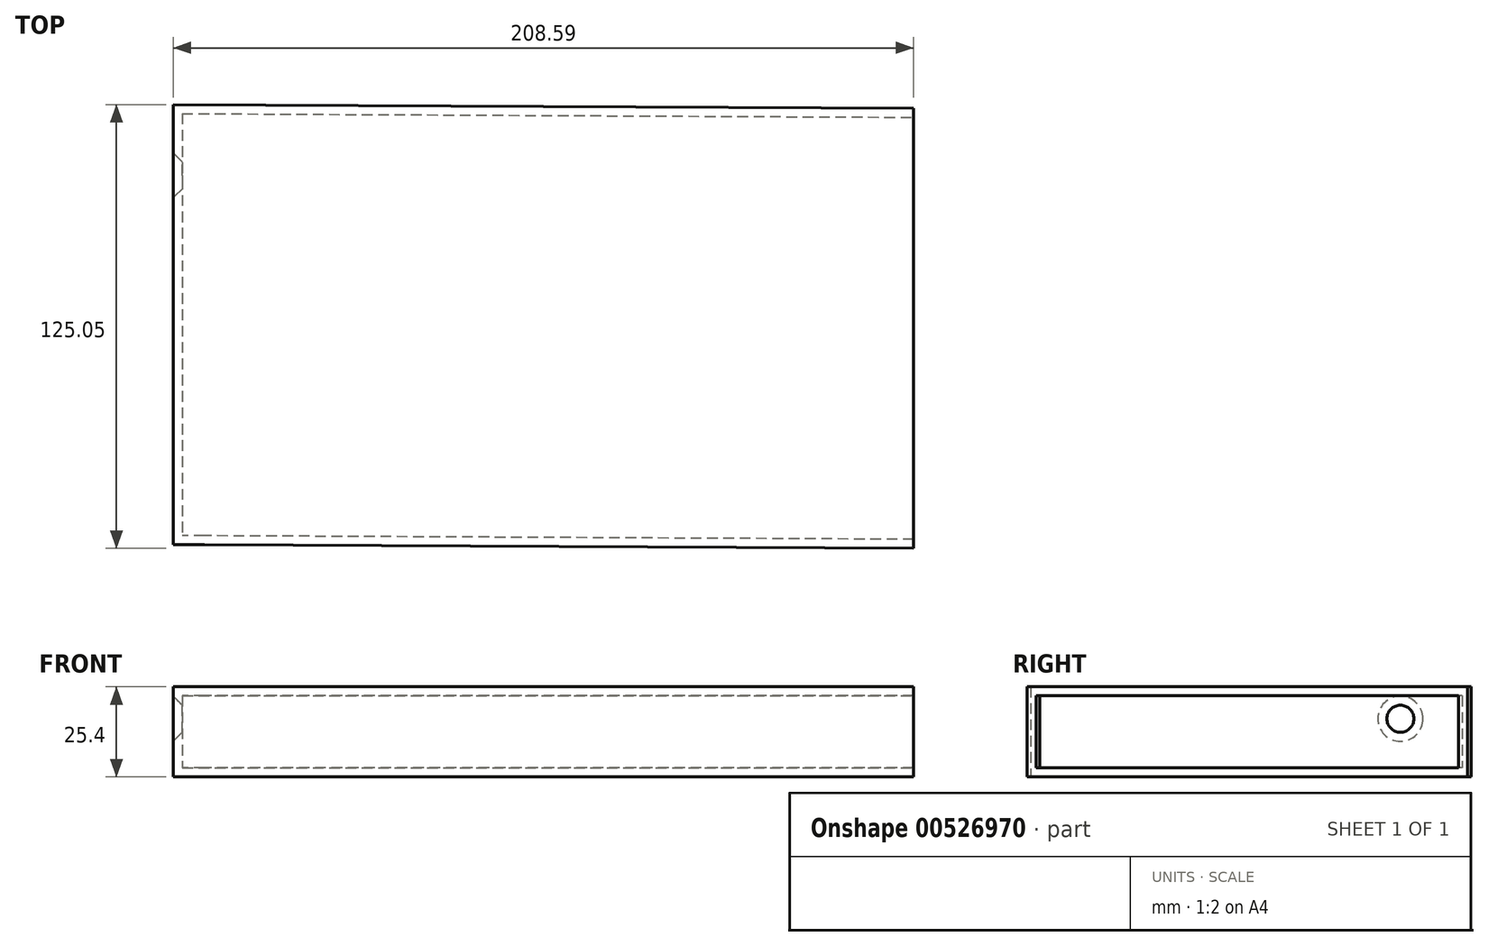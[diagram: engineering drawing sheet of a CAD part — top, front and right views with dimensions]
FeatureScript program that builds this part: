
annotation { "Feature Type Name" : "Feature", "Feature Type Description" : "" }
export const myFeature = defineFeature(function(context is Context, id is Id, definition is map)
    precondition{}
    {
        {
            var Q0;
            Q0=qCreatedBy(makeId("Top.planeOp"),FACE);
            var sketch = newSketch(context, id + "F0", { "sketchPlane" : qUnion([Q0])});
            skLineSegment(sketch, "E0", {"start": v(-113.31, 50.92) * mm, "end": v(95.28, 49.86) * mm});
            skLineSegment(sketch, "E1", {"start": v(95.28, 49.86) * mm, "end": v(95.28, -74.13) * mm});
            skLineSegment(sketch, "E2", {"start": v(95.28, -74.13) * mm, "end": v(-104.5, -73.11) * mm});
            skLineSegment(sketch, "E3", {"start": v(-113.31, 50.92) * mm, "end": v(-113.31, -73.11) * mm});
            skLineSegment(sketch, "E4", {"start": v(-104.5, -73.11) * mm, "end": v(-113.31, -73.11) * mm});
            skSolve(sketch);
        }
        {
            var Q0;
            Q0=makeQuery(id+"F0.imprint","IMPRINT",FACE,{"disambiguationData":[TD([[makeQuery(id+"F0.imprint","IMPRINT",EDGE,{"derivedFrom":sQuery(id+"F0.wireOp",EDGE,"E0")}),-1.0]])]});
            extrude(context, id + "F1", {"entities" : qUnion([Q0]), "depth" : 25.4 * mm, "offsetDistance" : 25.4 * mm});
        }
        {
            var Q0;
            Q0=makeQuery(id+"F1.opExtrude","SWEPT_FACE",FACE,{"disambiguationData":[OSD([sQuery(id+"F0.wireOp",EDGE,"E3")])]});
            var sketch = newSketch(context, id + "F2", { "sketchPlane" : qUnion([Q0])});
            skLineSegment(sketch, "E5.bottom", {"start": v(-16.6, 11.22) * mm, "end": v(-45.38, 11.22) * mm});
            skLineSegment(sketch, "E5.top", {"start": v(-16.6, 21.59) * mm, "end": v(-45.38, 21.59) * mm});
            skLineSegment(sketch, "E5.left", {"start": v(-16.6, 11.22) * mm, "end": v(-16.6, 21.59) * mm});
            skLineSegment(sketch, "E5.right", {"start": v(-45.38, 11.22) * mm, "end": v(-45.38, 21.59) * mm});
            skPoint(sketch, "E5.middle", {"position": v(-31, 16.4) * mm});
            skSolve(sketch);
        }
        {
            var Q0;
            Q0=makeQuery(id+"F1.opExtrude","SWEPT_FACE",FACE,{"disambiguationData":[OSD([sQuery(id+"F0.wireOp",EDGE,"E1")])]});
            shell(context, id + "F3", {"entities" : qUnion([Q0]), "thickness" : 2.54 * mm});
        }
        {
            var Q0;
            Q0=sQuery(id+"F2.wireOp",VERTEX,"E5.middle");
            var Q1;
            Q1=makeQuery(id+"F1.opExtrude","SWEPT_BODY",BODY,{"disambiguationData":[OSD([sQuery(id+"F0.wireOp",EDGE,"E0"),sQuery(id+"F0.wireOp",EDGE,"E1"),sQuery(id+"F0.wireOp",EDGE,"E2"),sQuery(id+"F0.wireOp",EDGE,"E3"),sQuery(id+"F0.wireOp",EDGE,"E4")])]});
            hole(context, id + "F4", {"style" : HoleStyle.C_SINK, "endStyle" : HoleEndStyle.BLIND, "holeDiameter" : 6.35 * mm, "cSinkDiameter" : 12.7 * mm, "cSinkAngle" : 90 * degree, "holeDepth" : 12.7 * mm, "isTappedThrough" : true, "tappedDepth" : 12.7 * mm, "tapClearance" : 3, "locations" : qUnion([Q0]), "scope" : qUnion([Q1])});
        }
    });
